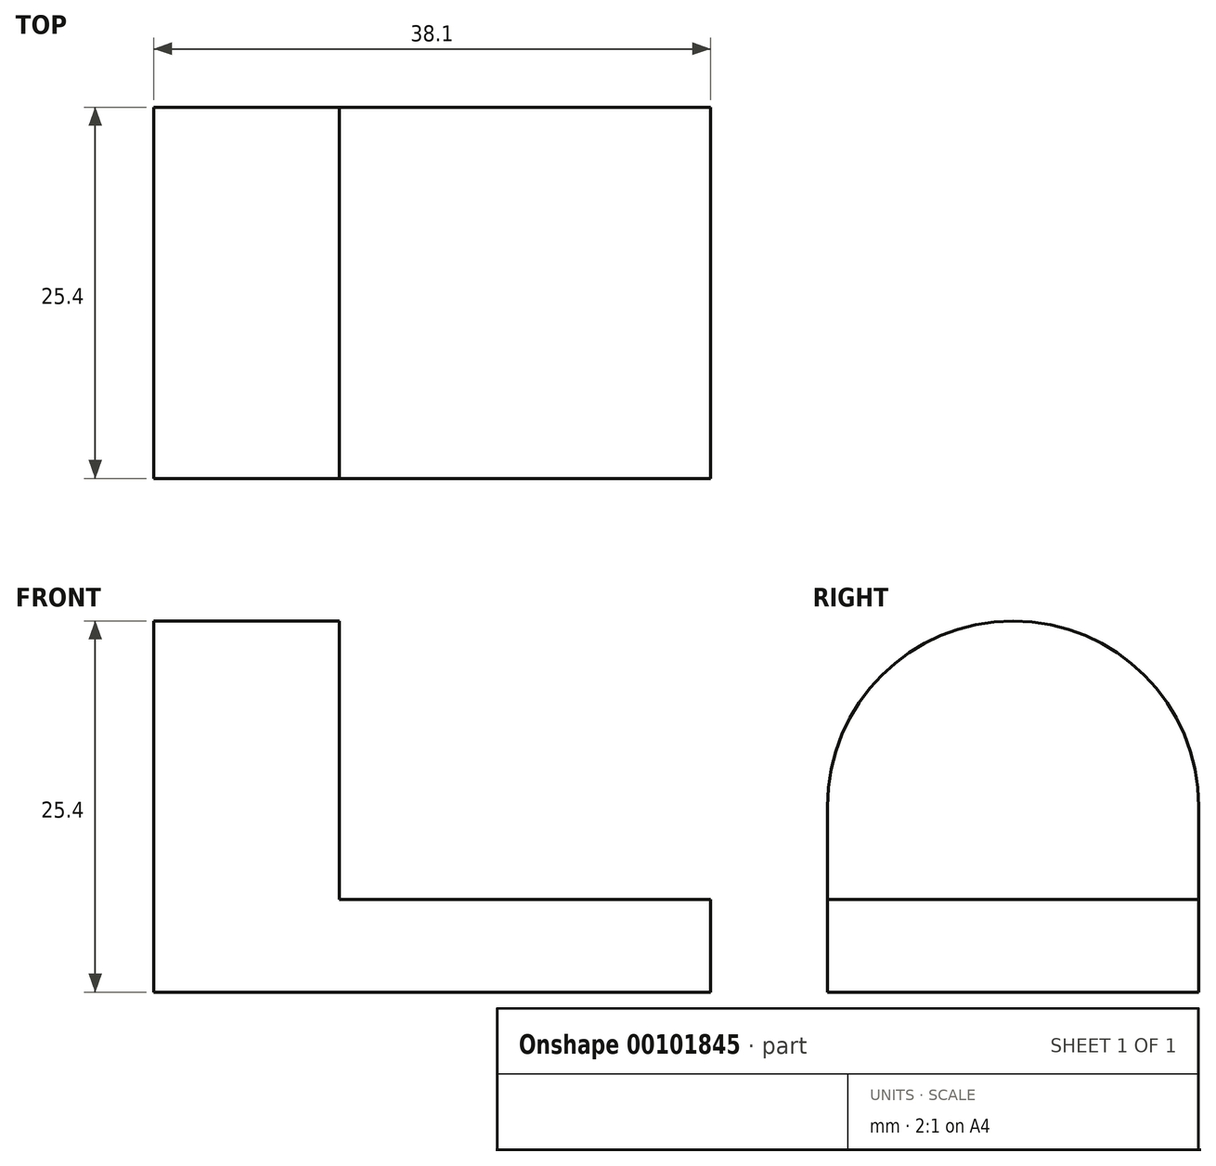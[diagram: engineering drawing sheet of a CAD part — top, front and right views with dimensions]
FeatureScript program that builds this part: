
annotation { "Feature Type Name" : "Feature", "Feature Type Description" : "" }
export const myFeature = defineFeature(function(context is Context, id is Id, definition is map)
    precondition{}
    {
        {
            var Q0;
            Q0=qCreatedBy(makeId("Front.planeOp"),FACE);
            var sketch = newSketch(context, id + "F0", { "sketchPlane" : qUnion([Q0])});
            skLineSegment(sketch, "E0", {"start": v(0, 0) * mm, "end": v(0, 25.4) * mm});
            skLineSegment(sketch, "E1", {"start": v(0, 25.4) * mm, "end": v(12.7, 25.4) * mm});
            skLineSegment(sketch, "E2", {"start": v(12.7, 25.4) * mm, "end": v(12.7, 6.35) * mm});
            skLineSegment(sketch, "E3", {"start": v(12.7, 6.35) * mm, "end": v(38.1, 6.35) * mm});
            skLineSegment(sketch, "E4", {"start": v(38.1, 6.35) * mm, "end": v(38.1, 0) * mm});
            skLineSegment(sketch, "E5", {"start": v(38.1, 0) * mm, "end": v(0, 0) * mm});
            skSolve(sketch);
        }
        {
            var Q0;
            Q0 = qSketchRegion(id + "F0", true);
            extrude(context, id + "F1", {"entities" : qUnion([Q0]), "depth" : 25.4 * mm});
        }
        {
            var Q0;
            Q0=makeQuery(id+"F1.opExtrude","SWEPT_FACE",FACE,{"disambiguationData":[OSD([sQuery(id+"F0.wireOp",EDGE,"E0")])]});
            var sketch = newSketch(context, id + "F2", { "sketchPlane" : qUnion([Q0])});
            skArc(sketch, "E6", {"start": v(25.4, 12.7) * mm, "mid": v(12.7, 25.4) * mm, "end": v(0, 12.7) * mm});
            skSolve(sketch);
        }
        {
            var Q0;
            {var subQ0=sQuery(id+"F2.wireOp",EDGE,"E6");var subQ1=sQuery(id+"F0.wireOp",EDGE,"E0");var subQ2=makeQuery(id+"F1.opExtrude","CAP_EDGE",EDGE,{"disambiguationData":[OSD([subQ1])],"isStart":true});var subQ3=makeQuery(id+"F2.imprint","INTERSECT",VERTEX,{"derivedFrom":[subQ2,subQ0]});Q0=makeQuery(id+"F2.imprint","IMPRINT",FACE,{"disambiguationData":[TD([[makeQuery(id+"F2.imprint","IMPRINT",EDGE,{"disambiguationData":[TD([[subQ3,1.0]])],"derivedFrom":subQ0}),-1.0]])]});}
            var Q1;
            {var subQ0=sQuery(id+"F2.wireOp",EDGE,"E6");var subQ1=sQuery(id+"F0.wireOp",EDGE,"E0");var subQ2=makeQuery(id+"F1.opExtrude","CAP_EDGE",EDGE,{"disambiguationData":[OSD([subQ1])],"isStart":false});var subQ3=makeQuery(id+"F2.imprint","INTERSECT",VERTEX,{"derivedFrom":[subQ2,subQ0]});Q1=makeQuery(id+"F2.imprint","IMPRINT",FACE,{"disambiguationData":[TD([[makeQuery(id+"F2.imprint","IMPRINT",EDGE,{"disambiguationData":[TD([[subQ3,-1.0]])],"derivedFrom":subQ0}),-1.0]])]});}
            extrude(context, id + "F3", {"entities" : qUnion([Q0, Q1]), "operationType" : NewBodyOperationType.REMOVE, "endBound" : BoundingType.THROUGH_ALL, "oppositeDirection" : true, "depth" : 12.7 * mm});
        }
    });
